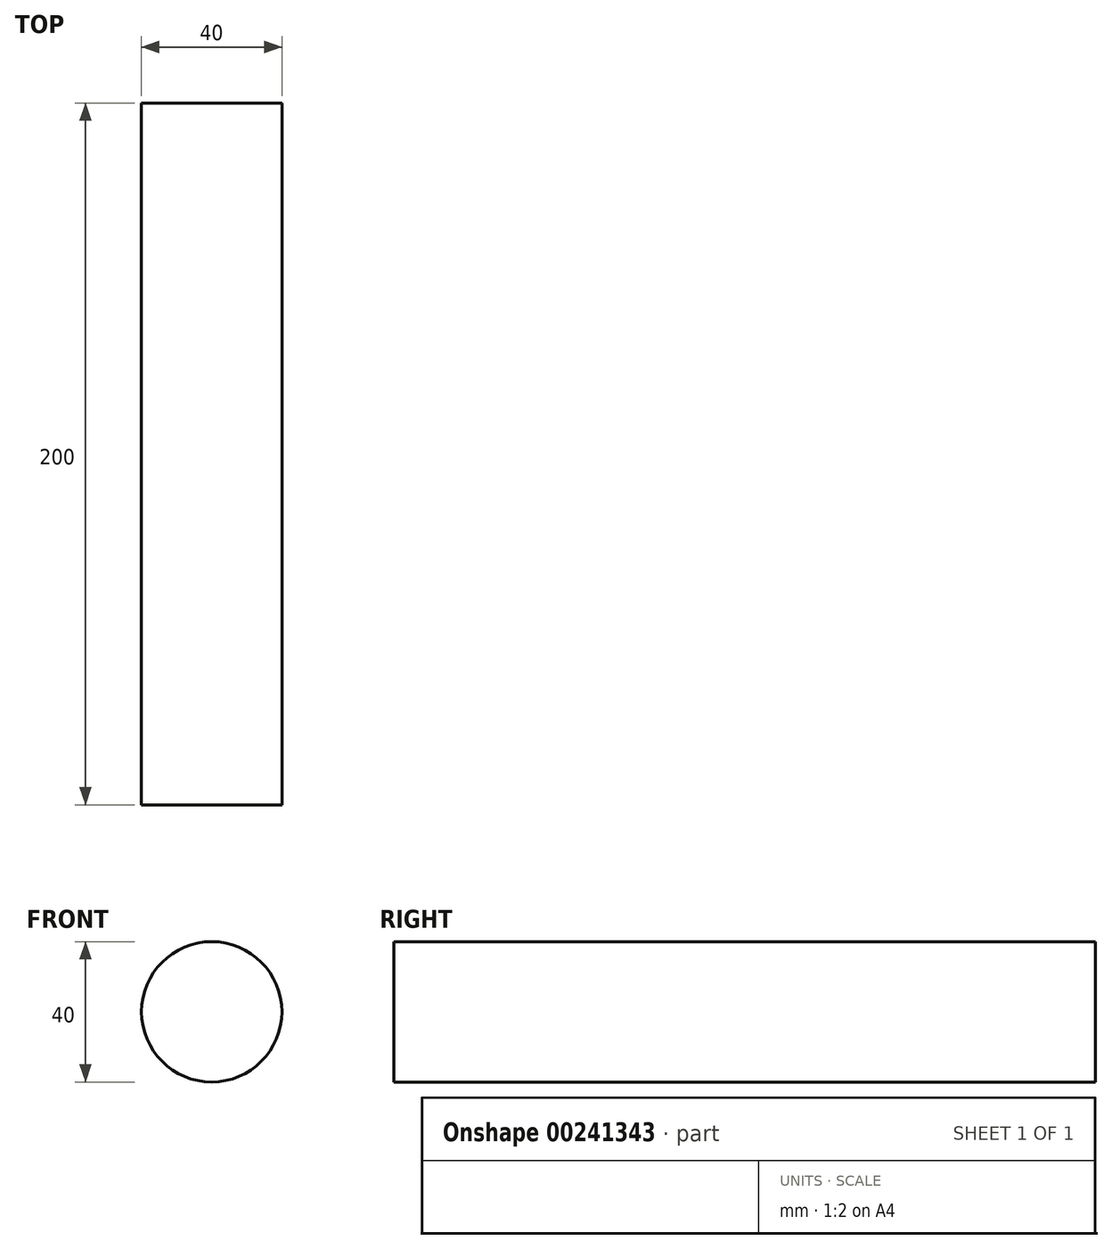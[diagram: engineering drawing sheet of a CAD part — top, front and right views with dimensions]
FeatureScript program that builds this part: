
annotation { "Feature Type Name" : "Feature", "Feature Type Description" : "" }
export const myFeature = defineFeature(function(context is Context, id is Id, definition is map)
    precondition{}
    {
        {
            var Q0;
            Q0=qCreatedBy(makeId("Front.planeOp"),FACE);
            var sketch = newSketch(context, id + "F0", { "sketchPlane" : qUnion([Q0])});
            skCircle(sketch, "E0", {"center": v(0, 0) * mm, "radius": 20 * mm});
            skSolve(sketch);
        }
        {
            var Q0;
            Q0 = qSketchRegion(id + "F0", true);
            extrude(context, id + "F1", {"entities" : qUnion([Q0]), "depth" : 200 * mm, "offsetDistance" : 25 * mm});
        }
    });
